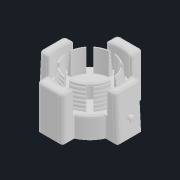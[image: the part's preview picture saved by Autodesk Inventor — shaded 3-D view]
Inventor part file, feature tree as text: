
AUTODESK INVENTOR PART (.ipt)
format: ipt  version: 2021.3 (Build 253353000, 353)  size: 1,809,408 bytes
history: native  units: mm
features: extrude x7, sketch x7, fillet x5, draft x2, helix x2, direct_edit x1, hole x1, pattern_circular x1, chamfer x1, projected_geometry x1, other x1
ambient origin geometry x8: Origin, YZ Plane, XZ Plane, XY Plane, X Axis, Y Axis, Z Axis, Center Point
bodies: Solid1 (feature_tree)
feature tree (29):
  extrude  "Extrusion1"  Depth=26.5mm
  draft  "FaceDraft1"
  sketch  "Sketch2"  dims[d34=0.0mm d35=0.0mm]
  helix  "Coil3"  [1 undecoded]
  helix  "Coil4"  [1 undecoded]
  direct_edit  "Direct Edit2"
  extrude  "Extrusion2"  Depth=12.0mm TaperAngle=0.0deg
  sketch  "Sketch4"  dims[d44=12.8mm d45=0.0mm d56=8.726646mm]
  extrude  "Extrusion3"  Depth=8.726646mm
  extrude  "Extrusion4"  TaperAngle=90.0deg  [1 undecoded]
  extrude  "Extrusion8"  Depth=0.8mm
  hole  "Hole1"  [1 undecoded]
  sketch  "Sketch9"  dims[d79=-0.127mm d82=3.0mm d83=3.0mm d84=1.5mm d85=1.5mm d86=0.0mm d87=0.0mm d91=3.0mm d92=3.0mm d93=1.5mm d94=1.5mm d95=5.3mm d96=6.0mm d97=10.0mm d98=10.0mm d99=90.0deg d100=8.0mm d101=20.594885mm d108=35.6mm d110=3.15mm d113=1.575mm d114=7.45mm d115=2.35mm d117=3.6mm d118=0.0mm d119=1.2mm d120=0.0mm d121=20.0mm d122=360.0deg d126=1.0mm d129=0.3mm d130=2.0mm d131=45.0deg d133=14.65mm d134=14.65mm d136=14.7mm d137=23.15mm d138=46.3mm d139=46.3mm d140=0.523599mm d141=1.0mm d142=1.0mm d143=2.0mm d144=0.8mm d109=0.5mm d111=0.5mm d112=0.872665mm]
  extrude  "Extrusion11"  Depth=0.8mm
  extrude  "Extrusion12"  Depth=0.8mm
  pattern_circular  "Circular Pattern1"  [2 undecoded]
  fillet  "Fillet4"  Radius=3.0mm
  chamfer  "Chamfer2"  Distance=3.0mm
  draft  "FaceDraft5"
  fillet  "Fillet6"  Radius=1.5mm
  fillet  "Fillet7"  Radius=1.5mm
  fillet  "Fillet8"  Radius=35.6mm
  fillet  "Fillet9"  Radius=3.15mm
  sketch  "Sketch1"  dims[d0=25.0mm d1=26.5mm d2=12.875mm d3=0.0mm d4=1.047198mm]
  sketch  "Sketch3"  dims[d36=7.325mm d37=7.0mm d38=7.325mm d39=0.0mm d40=7.0mm d41=28.73603mm d42=12.0mm d43=0.0mm]
  sketch  "Sketch5"  dims[d62=2.0mm d63=13.0mm d64=10.0mm d65=1.047198mm]
  sketch  "Sketch7"  dims[d66=90.0deg d67=90.0deg d68=0.0mm d69=0.0mm d70=2.0mm d71=3.0mm d72=10.0mm d73=-1.047198mm d74=90.0deg d75=90.0deg d76=0.0mm d77=0.0mm]
  projected_geometry  "Projected Loop1"
  other  "Size2"
note: 6 required parameter values undecoded (feature->parameter linkage not recoverable at this tier; creation-order binding heuristic only, values carry confidence <= 0.55)
